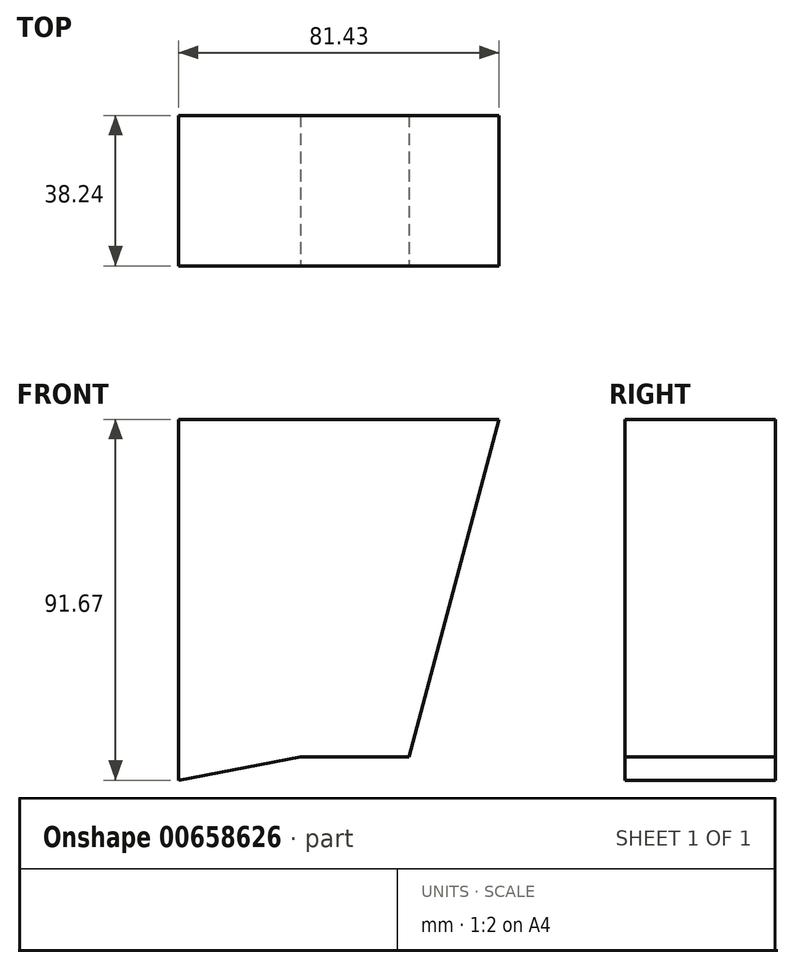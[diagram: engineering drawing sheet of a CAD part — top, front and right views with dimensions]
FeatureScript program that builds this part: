
annotation { "Feature Type Name" : "Feature", "Feature Type Description" : "" }
export const myFeature = defineFeature(function(context is Context, id is Id, definition is map)
    precondition{}
    {
        {
            var Q0;
            Q0=qCreatedBy(makeId("Front.planeOp"),FACE);
            var sketch = newSketch(context, id + "F0", { "sketchPlane" : qUnion([Q0])});
            skLineSegment(sketch, "E0", {"start": v(-58.5, -46.76) * mm, "end": v(-58.5, 44.9) * mm});
            skLineSegment(sketch, "E1", {"start": v(-58.5, 44.9) * mm, "end": v(22.94, 44.9) * mm});
            skLineSegment(sketch, "E2", {"start": v(22.94, 44.9) * mm, "end": v(0, -40.83) * mm});
            skLineSegment(sketch, "E3", {"start": v(0, -40.83) * mm, "end": v(-27.46, -40.83) * mm});
            skLineSegment(sketch, "E4", {"start": v(-27.46, -40.83) * mm, "end": v(-58.5, -46.76) * mm});
            skSolve(sketch);
        }
        {
            var Q0;
            Q0=sQuery(id+"F0.wireOp",EDGE,"E4");
            var Q1;
            Q1=sQuery(id+"F0.wireOp",EDGE,"E0");
            var Q2;
            Q2=sQuery(id+"F0.wireOp",EDGE,"E2");
            var Q3;
            Q3=sQuery(id+"F0.wireOp",EDGE,"E3");
            var Q4;
            Q4=sQuery(id+"F0.wireOp",EDGE,"E1");
            extrude(context, id + "F1", {"bodyType" : ToolBodyType.SURFACE, "surfaceEntities" : qUnion([Q0, Q1, Q2, Q3, Q4]), "depth" : 38.24 * mm, "offsetDistance" : 25.4 * mm});
        }
    });
